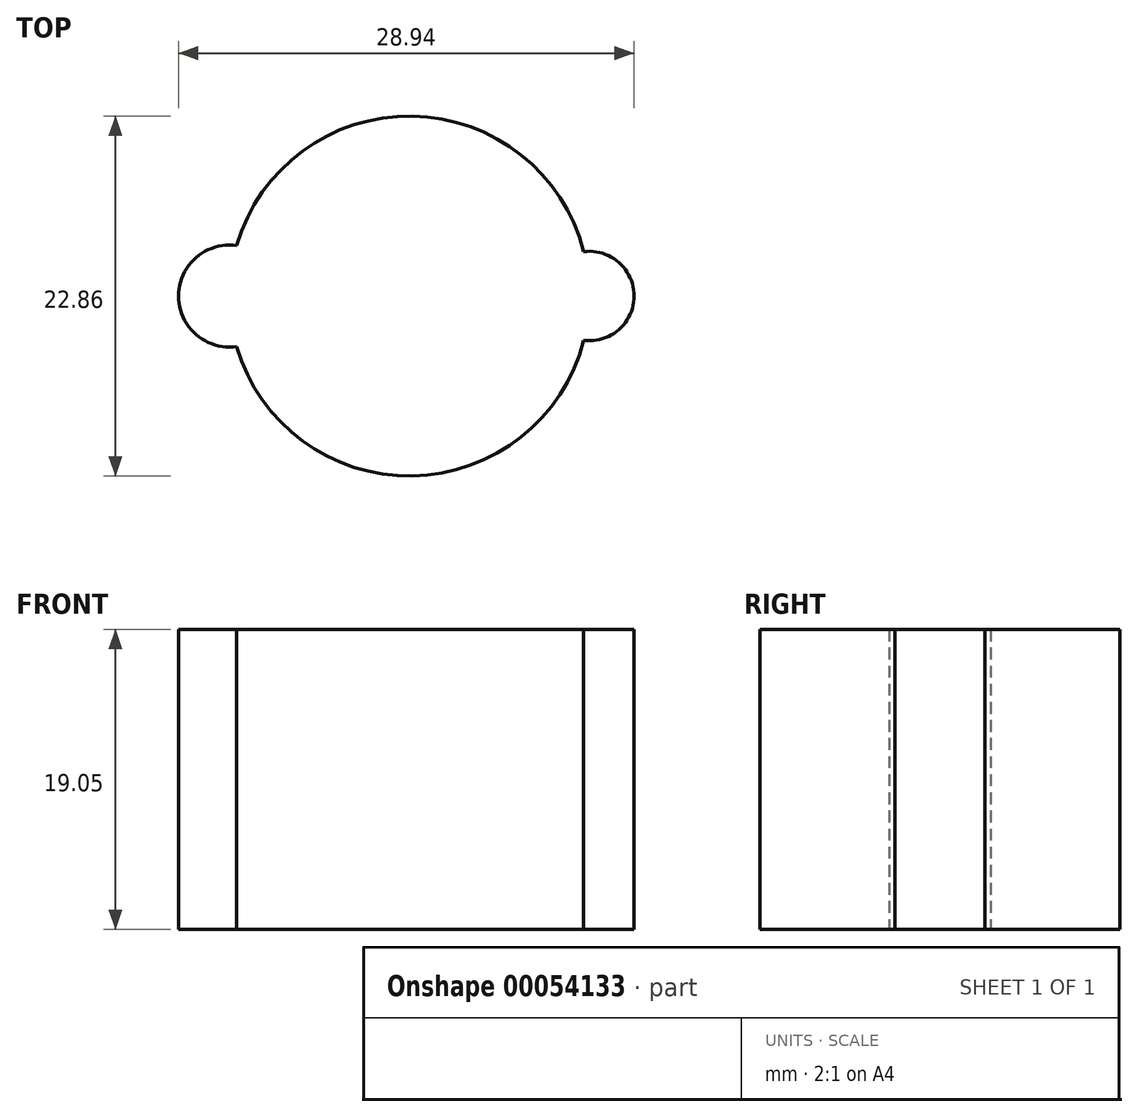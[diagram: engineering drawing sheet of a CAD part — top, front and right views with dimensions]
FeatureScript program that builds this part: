
annotation { "Feature Type Name" : "Feature", "Feature Type Description" : "" }
export const myFeature = defineFeature(function(context is Context, id is Id, definition is map)
    precondition{}
    {
        {
            var Q0;
            Q0=qCreatedBy(makeId("Top.planeOp"),FACE);
            var sketch = newSketch(context, id + "F0", { "sketchPlane" : qUnion([Q0])});
            skPoint(sketch, "E0.center.orphan", {"position": v(-0.47, 0) * mm});
            skCircle(sketch, "E1", {"center": v(0, 0) * mm, "radius": 11.43 * mm});
            skCircle(sketch, "E2", {"center": v(-11.43, 0) * mm, "radius": 3.24 * mm});
            skCircle(sketch, "E3", {"center": v(11.43, 0) * mm, "radius": 2.84 * mm});
            skSolve(sketch);
        }
        {
            var Q0;
            Q0 = qSketchRegion(id + "F0", true);
            extrude(context, id + "F1", {"entities" : qUnion([Q0]), "depth" : 12.7 * mm});
        }
        {
            var Q0;
            Q0 = qSketchRegion(id + "F0", true);
            extrude(context, id + "F2", {"entities" : qUnion([Q0]), "operationType" : NewBodyOperationType.ADD, "depth" : 19.05 * mm});
        }
    });
